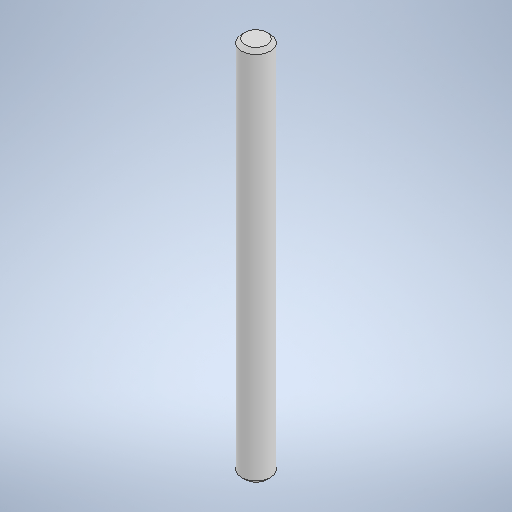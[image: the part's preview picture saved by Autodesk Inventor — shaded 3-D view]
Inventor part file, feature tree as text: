
AUTODESK INVENTOR PART (.ipt)
format: ipt  version: 2025.1 (Build 291241000, 241)  size: 247,808 bytes
history: native  units: mm
features: extrude x1, chamfer x1, sketch x1
ambient origin geometry x8: Origin, YZ Plane, XZ Plane, XY Plane, X Axis, Y Axis, Z Axis, Center Point
bodies: Solid1 (feature_tree)
feature tree (3):
  extrude  "Extrusion1"  Depth=26.0mm TaperAngle=0.0deg
  chamfer  "Chamfer1"  Distance=0.25mm Angle=45.0deg
  sketch  "Sketch1"  dims[d0=2.0mm d1=26.0mm d2=0.0mm d3=0.25mm d4=2.0mm d5=45.0deg]
